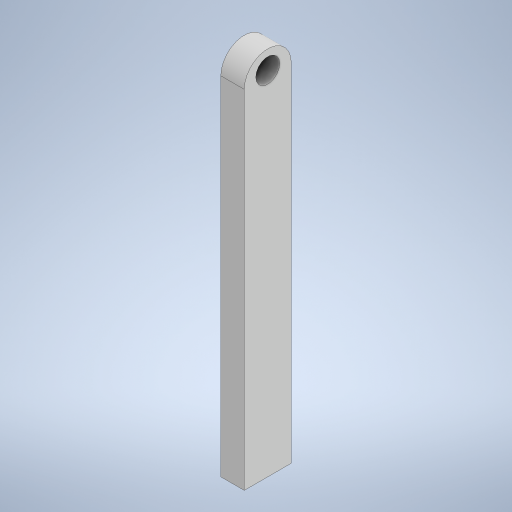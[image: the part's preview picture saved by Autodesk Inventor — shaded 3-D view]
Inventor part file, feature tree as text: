
AUTODESK INVENTOR PART (.ipt)
format: ipt  version: 2023 (Build 270158000, 158)  size: 242,688 bytes
history: native  units: mm
features: sketch x2, extrude x1, hole x1, fillet x1
ambient origin geometry x8: Origin, YZ Plane, XZ Plane, XY Plane, X Axis, Y Axis, Z Axis, Center Point
bodies: Volumenkörper1 (feature_tree)
feature tree (5):
  extrude  "Extrusion1"  Depth=20.0mm
  hole  "Bohrung1"  [1 undecoded]
  fillet  "Rundung1"  Radius=10.0mm
  sketch  "Skizze1"  dims[d0=158.0mm d1=20.0mm]
  sketch  "Skizze2"  dims[d2=10.0mm d3=0.0mm d4=10.2mm d5=6.0mm d6=4.0mm d7=2.0mm d8=90.0deg d9=8.0mm d10=20.594885mm d11=150.0mm d12=10.0mm d13=10.0mm]
note: 1 required parameter value undecoded (feature->parameter linkage not recoverable at this tier; creation-order binding heuristic only, values carry confidence <= 0.55)
